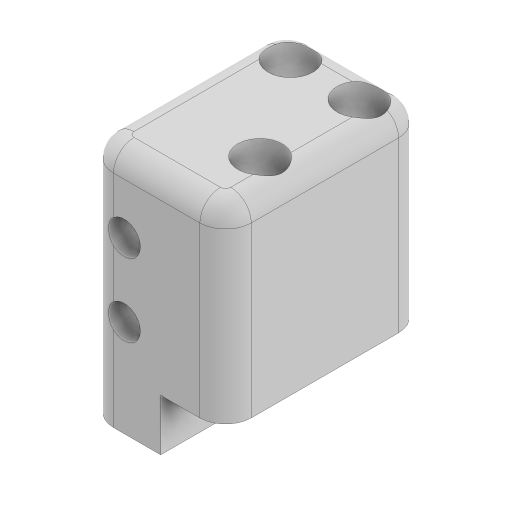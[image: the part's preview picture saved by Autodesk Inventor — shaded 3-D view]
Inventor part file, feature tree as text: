
AUTODESK INVENTOR PART (.ipt)
format: ipt  version: 2024 (Build 280153000, 153)  size: 305,664 bytes
history: native  units: in
note: dims shown in document units (in); Inventor stores cm internally (conversion verified against a paired STEP export)
features: extrude x3, sketch x3, fillet x2, projected_geometry x1
ambient origin geometry x8: Origin, YZ Plane, XZ Plane, XY Plane, X Axis, Y Axis, Z Axis, Center Point
bodies: Solid1 (feature_tree)
feature tree (9):
  extrude  "Extrusion1"  Depth=0.92in TaperAngle=0.0deg
  extrude  "Extrusion2"  Depth=0.1in
  fillet  "Fillet1"  Radius=0.2165in
  fillet  "Fillet2"  Radius=0.2165in
  extrude  "Extrusion3"  Depth=0.625in TaperAngle=0.0deg
  sketch  "Sketch1"  dims[d0=0.65in d1=0.0in d2=0.92in d3=0.0in]
  sketch  "Sketch2"  dims[d4=0.125in d5=0.1in d6=0.2165in d7=0.2165in]
  projected_geometry  "Projected Loop1"
  sketch  "Sketch3"  dims[d8=0.2165in d9=0.625in d10=0.0in]
